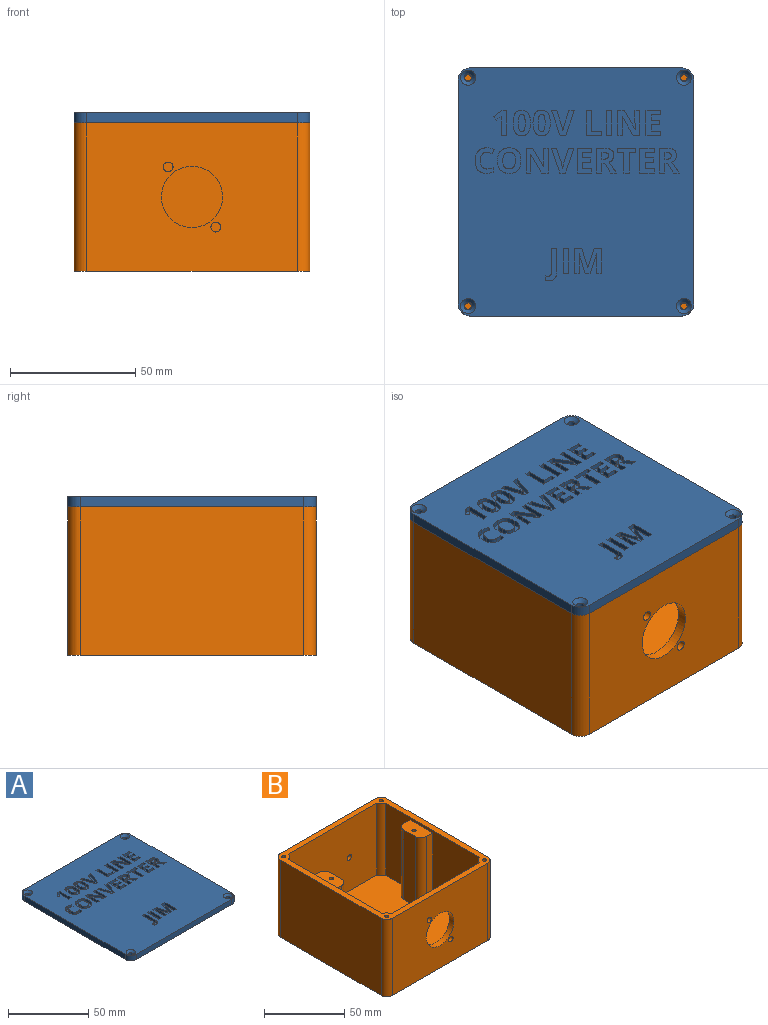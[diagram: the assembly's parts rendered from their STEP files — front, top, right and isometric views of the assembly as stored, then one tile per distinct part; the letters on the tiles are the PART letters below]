
ASSEMBLY  parts=2 mates=1
PART A: 287 faces, bbox 94x99x4 mm
  f0: plane 99x94mm, normal (0,0,1), area 8303.9mm2, adj f1,f2,f3,f8,f10,f11,f12,f13
  f1: plane 84x4mm, normal (0,1,0), area 336mm2, adj f0,f9,f10,f13
  f2: plane 89x4mm, normal (-1,0,0), area 356mm2, adj f0,f9,f10,f11
  f3: plane 84x4mm, normal (0,-1,0), area 336mm2, adj f0,f9,f11,f12
  f4: cylinder r=1.5mm len=3mm, axis (0,0,-1), area 23.6mm2, adj f9,f17
  f5: cylinder r=1.5mm len=3mm, axis (0,0,-1), area 23.6mm2, adj f9,f14
  f6: cylinder r=1.5mm len=3mm, axis (0,0,-1), area 23.6mm2, adj f9,f15
  f7: cylinder r=1.5mm len=3mm, axis (0,0,-1), area 23.6mm2, adj f9,f16
  f8: plane 89x4mm, normal (1,0,0), area 356mm2, adj f0,f9,f12,f13
  f9: plane 99x94mm, normal (0,0,-1), area 9256.3mm2, adj f1,f2,f3,f4,f5,f6,f7,f8
  f10: cylinder r=5mm len=5mm, axis (0,0,1), area 31.4mm2, adj f0,f1,f2,f9
  f11: cylinder r=5mm len=5mm, axis (0,0,-1), area 31.4mm2, adj f0,f2,f3,f9
  f12: cylinder r=5mm len=5mm, axis (0,0,1), area 31.4mm2, adj f0,f3,f8,f9
  f13: cylinder r=5mm len=5mm, axis (0,0,-1), area 31.4mm2, adj f0,f1,f8,f9
  f14: cone r=1.5mm half-angle=45deg, axis (0,0,1), area 30mm2, adj f0,f5
  f15: cone r=1.5mm half-angle=45deg, axis (0,0,1), area 30mm2, adj f0,f6
  f16: cone r=1.5mm half-angle=45deg, axis (0,0,1), area 30mm2, adj f0,f7
  f17: cone r=1.5mm half-angle=45deg, axis (0,0,1), area 30mm2, adj f0,f4
  f18: extruded ~2.18x2mm, area 4.5mm2, adj f0,f19,f27,f28
  f19: extruded ~2x0.97mm, area 2mm2, adj f0,f18,f20,f28
  f20: extruded ~2x1.22mm, area 2.5mm2, adj f0,f19,f21,f28
  f21: plane 5.9x2mm, normal (-0.95,-0.3,0), area 12.4mm2, adj f0,f20,f22,f28
  f22: plane 2.12x2mm, normal (0,-1,0), area 4.2mm2, adj f0,f21,f23,f28
  f23: plane 9.92x3.36mm, normal (0.95,0.32,0), area 20.9mm2, adj f0,f22,f24,f28
  f24: plane 2.29x2mm, normal (0,1,0), area 4.6mm2, adj f0,f23,f25,f28
  f25: plane 9.92x3.37mm, normal (-0.95,0.32,0), area 20.9mm2, adj f0,f24,f26,f28
  f26: plane 2.12x2mm, normal (0,-1,0), area 4.2mm2, adj f0,f25,f27,f28
  f27: plane 5.9x2mm, normal (0.95,-0.3,0), area 12.4mm2, adj f0,f18,f26,f28
  f28: plane 9.92x9.03mm, normal (0,0,1), area 37.9mm2, adj f18,f19,f20,f21,f22,f23,f24,f25
  f29: plane 2x1.72mm, normal (0,-1,0), area 3.4mm2, adj f0,f30,f38,f39
  f30: plane 3.19x2.54mm, normal (0.62,-0.78,0), area 8.2mm2, adj f0,f29,f31,f39
  f31: plane 2x1.26mm, normal (0.78,0.63,0), area 3.2mm2, adj f0,f30,f32,f39
  f32: plane 2x1.14mm, normal (-0.63,0.78,0), area 2.9mm2, adj f0,f31,f33,f39
  f33: extruded ~2x0.73mm, area 2mm2, adj f0,f32,f34,f39
  f34: plane 2x1.03mm, normal (1,-0.03,0), area 2.1mm2, adj f0,f33,f35,f39
  f35: plane 2x0.94mm, normal (1,-0.02,0), area 1.9mm2, adj f0,f34,f36,f39
  f36: plane 5.74x2mm, normal (1,0,0), area 11.5mm2, adj f0,f35,f37,f39
  f37: plane 2.1x2mm, normal (0,1,0), area 4.2mm2, adj f0,f36,f38,f39
  f38: plane 9.92x2mm, normal (-1,0,0), area 19.8mm2, adj f0,f29,f37,f39
  f39: plane 9.92x4.92mm, normal (0,0,1), area 25.4mm2, adj f29,f30,f31,f32,f33,f34,f35,f36
  f40: plane 3.8x2.37mm, normal (0.85,0.53,0), area 9mm2, adj f0,f41,f57,f59
  f41: plane 2.33x2mm, normal (0,1,0), area 4.7mm2, adj f0,f40,f42,f59
  f42: extruded ~4.32x2.92mm, area 10.4mm2, adj f0,f41,f43,f59
  f43: extruded ~2x1.36mm, area 3.5mm2, adj f0,f42,f44,f59
  f44: extruded ~2x1.56mm, area 3.3mm2, adj f0,f43,f45,f59
  f45: extruded ~2.24x2mm, area 5.1mm2, adj f0,f44,f46,f59
  f46: extruded ~2.99x2mm, area 6.3mm2, adj f0,f45,f47,f59
  f47: plane 2.89x2mm, normal (0,-1,0), area 5.8mm2, adj f0,f46,f48,f59
  f48: plane 9.92x2mm, normal (1,0,0), area 19.8mm2, adj f0,f47,f49,f59
  f49: plane 2.1x2mm, normal (0,1,0), area 4.2mm2, adj f0,f48,f50,f59
  f50: plane 3.8x2mm, normal (-1,0,0), area 7.6mm2, adj f0,f49,f57,f59
  f51: plane 2x0.64mm, normal (0,1,0), area 1.3mm2, adj f52,f58,f59,f285
  f52: extruded ~2x1.5mm, area 3.1mm2, adj f51,f53,f59,f285
  f53: extruded ~2x1mm, area 2.3mm2, adj f52,f54,f59,f285
  f54: extruded ~2x1.04mm, area 2.4mm2, adj f53,f55,f59,f285
  f55: extruded ~2x1.47mm, area 3.1mm2, adj f54,f56,f59,f285
  f56: plane 2x0.68mm, normal (0,-1,0), area 1.4mm2, adj f55,f58,f59,f285
  f57: plane 2x1.12mm, normal (0,1,0), area 2.2mm2, adj f0,f40,f50,f59
  f58: plane 2.68x2mm, normal (-1,0,0), area 5.4mm2, adj f51,f56,f59,f285
  f59: plane 9.92x7.92mm, normal (0,0,1), area 48mm2, adj f40,f41,f42,f43,f44,f45,f46,f47
  f60: plane 3.8x2.37mm, normal (0.85,0.53,0), area 9mm2, adj f0,f61,f77,f79
  f61: plane 2.33x2mm, normal (0,1,0), area 4.7mm2, adj f0,f60,f62,f79
  f62: extruded ~4.32x2.92mm, area 10.4mm2, adj f0,f61,f63,f79
  f63: extruded ~2x1.36mm, area 3.5mm2, adj f0,f62,f64,f79
  f64: extruded ~2x1.56mm, area 3.3mm2, adj f0,f63,f65,f79
  f65: extruded ~2.24x2mm, area 5.1mm2, adj f0,f64,f66,f79
  f66: extruded ~2.99x2mm, area 6.3mm2, adj f0,f65,f67,f79
  f67: plane 2.89x2mm, normal (0,-1,0), area 5.8mm2, adj f0,f66,f68,f79
  f68: plane 9.92x2mm, normal (1,0,0), area 19.8mm2, adj f0,f67,f69,f79
  f69: plane 2.1x2mm, normal (0,1,0), area 4.2mm2, adj f0,f68,f70,f79
  f70: plane 3.8x2mm, normal (-1,0,0), area 7.6mm2, adj f0,f69,f77,f79
  f71: plane 2x0.64mm, normal (0,1,0), area 1.3mm2, adj f72,f78,f79,f286
  f72: extruded ~2x1.5mm, area 3.1mm2, adj f71,f73,f79,f286
  f73: extruded ~2x1mm, area 2.3mm2, adj f72,f74,f79,f286
  f74: extruded ~2x1.04mm, area 2.4mm2, adj f73,f75,f79,f286
  f75: extruded ~2x1.47mm, area 3.1mm2, adj f74,f76,f79,f286
  f76: plane 2x0.68mm, normal (0,-1,0), area 1.4mm2, adj f75,f78,f79,f286
  f77: plane 2x1.12mm, normal (0,1,0), area 2.2mm2, adj f0,f60,f70,f79
  f78: plane 2.68x2mm, normal (-1,0,0), area 5.4mm2, adj f71,f76,f79,f286
  f79: plane 9.92x7.92mm, normal (0,0,1), area 48mm2, adj f60,f61,f62,f63,f64,f65,f66,f67
  f80: plane 2x1.74mm, normal (-1,0,0), area 3.5mm2, adj f0,f81,f85,f86
  f81: plane 4.02x2mm, normal (0,-1,0), area 8mm2, adj f0,f80,f82,f86
  f82: plane 8.18x2mm, normal (-1,0,0), area 16.4mm2, adj f0,f81,f83,f86
  f83: plane 2.1x2mm, normal (0,-1,0), area 4.2mm2, adj f0,f82,f84,f86
  f84: plane 9.92x2mm, normal (1,0,0), area 19.8mm2, adj f0,f83,f85,f86
  f85: plane 6.12x2mm, normal (0,1,0), area 12.2mm2, adj f0,f80,f84,f86
  f86: plane 9.92x6.12mm, normal (0,0,1), area 27.8mm2, adj f80,f81,f82,f83,f84,f85
  f87: plane 9.92x2mm, normal (-1,0,0), area 19.8mm2, adj f0,f88,f90,f91
  f88: plane 2.1x2mm, normal (0,-1,0), area 4.2mm2, adj f0,f87,f89,f91
  f89: plane 9.92x2mm, normal (1,0,0), area 19.8mm2, adj f0,f88,f90,f91
  f90: plane 2.1x2mm, normal (0,1,0), area 4.2mm2, adj f0,f87,f89,f91
  f91: plane 9.92x2.1mm, normal (0,0,1), area 20.9mm2, adj f87,f88,f89,f90
  f92: plane 2x1.89mm, normal (0,-1,0), area 3.8mm2, adj f0,f93,f105,f106
  f93: plane 4.69x2mm, normal (1,0,0), area 9.4mm2, adj f0,f92,f94,f106
  f94: extruded ~2.73x2mm, area 5.5mm2, adj f0,f93,f95,f106
  f95: plane 2x0.05mm, normal (0,-1,0), area 0.1mm2, adj f0,f94,f96,f106
  f96: plane 7.43x4.31mm, normal (-0.87,-0.5,0), area 17.2mm2, adj f0,f95,f97,f106
  f97: plane 2.65x2mm, normal (0,-1,0), area 5.3mm2, adj f0,f96,f98,f106
  f98: plane 9.92x2mm, normal (1,0,0), area 19.8mm2, adj f0,f97,f99,f106
  f99: plane 2x1.88mm, normal (0,1,0), area 3.8mm2, adj f0,f98,f100,f106
  f100: plane 4.67x2mm, normal (-1,0,0), area 9.3mm2, adj f0,f99,f101,f106
  f101: extruded ~2.83x2mm, area 5.7mm2, adj f0,f100,f102,f106
  f102: plane 2x0.06mm, normal (0,1,0), area 0.1mm2, adj f0,f101,f103,f106
  f103: plane 7.5x4.31mm, normal (0.87,0.5,0), area 17.3mm2, adj f0,f102,f104,f106
  f104: plane 2.67x2mm, normal (0,1,0), area 5.3mm2, adj f0,f103,f105,f106
  f105: plane 9.92x2mm, normal (-1,0,0), area 19.8mm2, adj f0,f92,f104,f106
  f106: plane 9.92x8.8mm, normal (0,0,1), area 55.7mm2, adj f92,f93,f94,f95,f96,f97,f98,f99
  f107: plane 3.61x2mm, normal (0,-1,0), area 7.2mm2, adj f0,f108,f118,f119
  f108: plane 2.56x2mm, normal (-1,0,0), area 5.1mm2, adj f0,f107,f109,f119
  f109: plane 3.36x2mm, normal (0,1,0), area 6.7mm2, adj f0,f108,f110,f119
  f110: plane 2x1.72mm, normal (-1,0,0), area 3.4mm2, adj f0,f109,f111,f119
  f111: plane 3.36x2mm, normal (0,-1,0), area 6.7mm2, adj f0,f110,f112,f119
  f112: plane 2.18x2mm, normal (-1,0,0), area 4.4mm2, adj f0,f111,f113,f119
  f113: plane 3.61x2mm, normal (0,1,0), area 7.2mm2, adj f0,f112,f114,f119
  f114: plane 2x1.72mm, normal (-1,0,0), area 3.4mm2, adj f0,f113,f115,f119
  f115: plane 5.71x2mm, normal (0,-1,0), area 11.4mm2, adj f0,f114,f116,f119
  f116: plane 9.92x2mm, normal (1,0,0), area 19.8mm2, adj f0,f115,f117,f119
  f117: plane 5.71x2mm, normal (0,1,0), area 11.4mm2, adj f0,f116,f118,f119
  f118: plane 2x1.74mm, normal (-1,0,0), area 3.5mm2, adj f0,f107,f117,f119
  f119: plane 9.92x5.71mm, normal (0,0,1), area 39.1mm2, adj f107,f108,f109,f110,f111,f112,f113,f114
  f120: extruded ~2x1.12mm, area 2.4mm2, adj f0,f121,f134,f135
  f121: plane 2x1.71mm, normal (-0.93,0.37,0), area 3.7mm2, adj f0,f120,f122,f135
  f122: extruded ~2.9x2mm, area 6mm2, adj f0,f121,f123,f135
  f123: extruded ~2.47x2mm, area 5.2mm2, adj f0,f122,f124,f135
  f124: extruded ~2x1.78mm, area 4.9mm2, adj f0,f123,f125,f135
  f125: extruded ~2.71x2mm, area 5.6mm2, adj f0,f124,f126,f135
  f126: extruded ~3.77x2mm, area 8mm2, adj f0,f125,f127,f135
  f127: extruded ~3.31x2mm, area 7.4mm2, adj f0,f126,f128,f135
  f128: extruded ~2.73x2mm, area 5.6mm2, adj f0,f127,f129,f135
  f129: plane 2x1.76mm, normal (-1,0,0), area 3.5mm2, adj f0,f128,f130,f135
  f130: extruded ~2.53x2mm, area 5.2mm2, adj f0,f129,f131,f135
  f131: extruded ~3.32x2.49mm, area 9.5mm2, adj f0,f130,f132,f135
  f132: extruded ~2.49x2mm, area 5.2mm2, adj f0,f131,f133,f135
  f133: extruded ~2x1.84mm, area 4.3mm2, adj f0,f132,f134,f135
  f134: extruded ~2x1.1mm, area 2.3mm2, adj f0,f120,f133,f135
  f135: plane 10.19x7.55mm, normal (0,0,1), area 34.5mm2, adj f120,f121,f122,f123,f124,f125,f126,f127
  f136: plane 2x1.89mm, normal (0,-1,0), area 3.8mm2, adj f0,f137,f149,f150
  f137: plane 4.69x2mm, normal (1,0,0), area 9.4mm2, adj f0,f136,f138,f150
  f138: extruded ~2.73x2mm, area 5.5mm2, adj f0,f137,f139,f150
  f139: plane 2x0.05mm, normal (0,-1,0), area 0.1mm2, adj f0,f138,f140,f150
  f140: plane 7.43x4.31mm, normal (-0.87,-0.5,0), area 17.2mm2, adj f0,f139,f141,f150
  f141: plane 2.65x2mm, normal (0,-1,0), area 5.3mm2, adj f0,f140,f142,f150
  f142: plane 9.92x2mm, normal (1,0,0), area 19.8mm2, adj f0,f141,f143,f150
  f143: plane 2x1.88mm, normal (0,1,0), area 3.8mm2, adj f0,f142,f144,f150
  f144: plane 4.67x2mm, normal (-1,0,0), area 9.3mm2, adj f0,f143,f145,f150
  f145: extruded ~2.83x2mm, area 5.7mm2, adj f0,f144,f146,f150
  f146: plane 2x0.06mm, normal (0,1,0), area 0.1mm2, adj f0,f145,f147,f150
  f147: plane 7.5x4.31mm, normal (0.87,0.5,0), area 17.3mm2, adj f0,f146,f148,f150
  f148: plane 2.67x2mm, normal (0,1,0), area 5.3mm2, adj f0,f147,f149,f150
  f149: plane 9.92x2mm, normal (-1,0,0), area 19.8mm2, adj f0,f136,f148,f150
  f150: plane 9.92x8.8mm, normal (0,0,1), area 55.7mm2, adj f136,f137,f138,f139,f140,f141,f142,f143
  f151: extruded ~2.18x2mm, area 4.5mm2, adj f0,f152,f160,f161
  f152: extruded ~2x0.97mm, area 2mm2, adj f0,f151,f153,f161
  f153: extruded ~2x1.22mm, area 2.5mm2, adj f0,f152,f154,f161
  f154: plane 5.9x2mm, normal (-0.95,-0.3,0), area 12.4mm2, adj f0,f153,f155,f161
  f155: plane 2.12x2mm, normal (0,-1,0), area 4.2mm2, adj f0,f154,f156,f161
  f156: plane 9.92x3.36mm, normal (0.95,0.32,0), area 20.9mm2, adj f0,f155,f157,f161
  f157: plane 2.29x2mm, normal (0,1,0), area 4.6mm2, adj f0,f156,f158,f161
  f158: plane 9.92x3.37mm, normal (-0.95,0.32,0), area 20.9mm2, adj f0,f157,f159,f161
  f159: plane 2.12x2mm, normal (0,-1,0), area 4.2mm2, adj f0,f158,f160,f161
  f160: plane 5.9x2mm, normal (0.95,-0.3,0), area 12.4mm2, adj f0,f151,f159,f161
  f161: plane 9.92x9.03mm, normal (0,0,1), area 37.9mm2, adj f151,f152,f153,f154,f155,f156,f157,f158
  f162: plane 3.61x2mm, normal (0,-1,0), area 7.2mm2, adj f0,f163,f173,f174
  f163: plane 2.56x2mm, normal (-1,0,0), area 5.1mm2, adj f0,f162,f164,f174
  f164: plane 3.36x2mm, normal (0,1,0), area 6.7mm2, adj f0,f163,f165,f174
  f165: plane 2x1.72mm, normal (-1,0,0), area 3.4mm2, adj f0,f164,f166,f174
  f166: plane 3.36x2mm, normal (0,-1,0), area 6.7mm2, adj f0,f165,f167,f174
  f167: plane 2.18x2mm, normal (-1,0,0), area 4.4mm2, adj f0,f166,f168,f174
  f168: plane 3.61x2mm, normal (0,1,0), area 7.2mm2, adj f0,f167,f169,f174
  f169: plane 2x1.72mm, normal (-1,0,0), area 3.4mm2, adj f0,f168,f170,f174
  f170: plane 5.71x2mm, normal (0,-1,0), area 11.4mm2, adj f0,f169,f171,f174
  f171: plane 9.92x2mm, normal (1,0,0), area 19.8mm2, adj f0,f170,f172,f174
  f172: plane 5.71x2mm, normal (0,1,0), area 11.4mm2, adj f0,f171,f173,f174
  f173: plane 2x1.74mm, normal (-1,0,0), area 3.5mm2, adj f0,f162,f172,f174
  f174: plane 9.92x5.71mm, normal (0,0,1), area 39.1mm2, adj f162,f163,f164,f165,f166,f167,f168,f169
  f175: plane 7.76x2.56mm, normal (-0.95,0.31,0), area 16.3mm2, adj f0,f176,f193,f194
  f176: plane 2x0.06mm, normal (0,1,0), area 0.1mm2, adj f0,f175,f177,f194
  f177: extruded ~2.3x2mm, area 4.6mm2, adj f0,f176,f178,f194
  f178: extruded ~2x0.77mm, area 1.5mm2, adj f0,f177,f179,f194
  f179: plane 4.69x2mm, normal (1,0,0), area 9.4mm2, adj f0,f178,f180,f194
  f180: plane 2x1.96mm, normal (0,1,0), area 3.9mm2, adj f0,f179,f181,f194
  f181: plane 9.92x2mm, normal (-1,0,0), area 19.8mm2, adj f0,f180,f182,f194
  f182: plane 2.86x2mm, normal (0,-1,0), area 5.7mm2, adj f0,f181,f183,f194
  f183: plane 7.58x2.49mm, normal (0.95,-0.31,0), area 16mm2, adj f0,f182,f184,f194
  f184: plane 2x0.04mm, normal (0,-1,0), area 0.1mm2, adj f0,f183,f185,f194
  f185: plane 7.58x2.35mm, normal (-0.96,-0.3,0), area 15.9mm2, adj f0,f184,f186,f194
  f186: plane 2.86x2mm, normal (0,-1,0), area 5.7mm2, adj f0,f185,f187,f194
  f187: plane 9.92x2mm, normal (1,0,0), area 19.8mm2, adj f0,f186,f188,f194
  f188: plane 2x1.88mm, normal (0,1,0), area 3.8mm2, adj f0,f187,f189,f194
  f189: plane 4.61x2mm, normal (-1,0,0), area 9.2mm2, adj f0,f188,f190,f194
  f190: extruded ~3.17x2mm, area 6.3mm2, adj f0,f189,f191,f194
  f191: plane 2x0.06mm, normal (0,1,0), area 0.1mm2, adj f0,f190,f192,f194
  f192: plane 7.78x2.39mm, normal (0.96,0.29,0), area 16.3mm2, adj f0,f191,f193,f194
  f193: plane 2x1.93mm, normal (0,1,0), area 3.9mm2, adj f0,f175,f192,f194
  f194: plane 10.6x9.92mm, normal (0,0,1), area 67.8mm2, adj f175,f176,f177,f178,f179,f180,f181,f182
  f195: extruded ~2x1.06mm, area 2.8mm2, adj f196,f209,f211,f212
  f196: extruded ~2x1.05mm, area 2.8mm2, adj f195,f197,f211,f212
  f197: extruded ~2.62x2mm, area 5.3mm2, adj f196,f198,f211,f212
  f198: extruded ~2.6x2mm, area 5.3mm2, adj f197,f199,f211,f212
  f199: extruded ~2x1.06mm, area 2.8mm2, adj f198,f200,f211,f212
  f200: extruded ~2x1.06mm, area 2.8mm2, adj f199,f201,f211,f212
  f201: extruded ~2.61x2mm, area 5.3mm2, adj f200,f209,f211,f212
  f202: extruded ~2.59x2mm, area 6.1mm2, adj f0,f203,f210,f211
  f203: extruded ~2.61x2mm, area 6mm2, adj f0,f202,f204,f211
  f204: extruded ~3.87x2mm, area 8mm2, adj f0,f203,f205,f211
  f205: extruded ~3.8x2mm, area 7.9mm2, adj f0,f204,f206,f211
  f206: extruded ~2.59x2mm, area 6mm2, adj f0,f205,f207,f211
  f207: extruded ~2.62x2mm, area 6.1mm2, adj f0,f206,f208,f211
  f208: extruded ~3.84x2mm, area 8mm2, adj f0,f207,f210,f211
  f209: extruded ~2.62x2mm, area 5.3mm2, adj f195,f201,f211,f212
  f210: extruded ~3.81x2mm, area 7.9mm2, adj f0,f202,f208,f211
  f211: plane 10.21x6.93mm, normal (0,0,1), area 43mm2, adj f195,f196,f197,f198,f199,f200,f201,f202
  f212: plane 6.82x2.76mm, normal (0,0,1), area 16mm2, adj f195,f196,f197,f198,f199,f200,f201,f209
  f213: extruded ~2x1.06mm, area 2.8mm2, adj f214,f227,f229,f230
  f214: extruded ~2x1.05mm, area 2.8mm2, adj f213,f215,f229,f230
  f215: extruded ~2.62x2mm, area 5.3mm2, adj f214,f216,f229,f230
  f216: extruded ~2.6x2mm, area 5.3mm2, adj f215,f217,f229,f230
  f217: extruded ~2x1.06mm, area 2.8mm2, adj f216,f218,f229,f230
  f218: extruded ~2x1.06mm, area 2.8mm2, adj f217,f219,f229,f230
  f219: extruded ~2.61x2mm, area 5.3mm2, adj f218,f227,f229,f230
  f220: extruded ~2.59x2mm, area 6.1mm2, adj f0,f221,f228,f229
  f221: extruded ~2.61x2mm, area 6mm2, adj f0,f220,f222,f229
  f222: extruded ~3.87x2mm, area 8mm2, adj f0,f221,f223,f229
  f223: extruded ~3.8x2mm, area 7.9mm2, adj f0,f222,f224,f229
  f224: extruded ~2.59x2mm, area 6mm2, adj f0,f223,f225,f229
  f225: extruded ~2.62x2mm, area 6.1mm2, adj f0,f224,f226,f229
  f226: extruded ~3.84x2mm, area 8mm2, adj f0,f225,f228,f229
  f227: extruded ~2.62x2mm, area 5.3mm2, adj f213,f219,f229,f230
  f228: extruded ~3.81x2mm, area 7.9mm2, adj f0,f220,f226,f229
  f229: plane 10.21x6.93mm, normal (0,0,1), area 43mm2, adj f213,f214,f215,f216,f217,f218,f219,f220
  f230: plane 6.82x2.76mm, normal (0,0,1), area 16mm2, adj f213,f214,f215,f216,f217,f218,f219,f227
  f231: extruded ~2x1.89mm, area 4.3mm2, adj f232,f243,f245,f246
  f232: extruded ~3.35x2.5mm, area 9.5mm2, adj f231,f233,f245,f246
  f233: extruded ~3.34x2.52mm, area 9.5mm2, adj f232,f234,f245,f246
  f234: extruded ~2x1.88mm, area 4.3mm2, adj f233,f235,f245,f246
  f235: extruded ~2.5x2mm, area 5.2mm2, adj f234,f243,f245,f246
  f236: extruded ~3.5x2mm, area 7.7mm2, adj f0,f237,f244,f245
  f237: extruded ~3.51x2mm, area 7.7mm2, adj f0,f236,f238,f245
  f238: extruded ~3.78x2mm, area 8.1mm2, adj f0,f237,f239,f245
  f239: extruded ~3.8x2mm, area 8.2mm2, adj f0,f238,f240,f245
  f240: extruded ~3.5x2mm, area 7.7mm2, adj f0,f239,f241,f245
  f241: extruded ~3.5x2mm, area 7.7mm2, adj f0,f240,f242,f245
  f242: extruded ~3.79x2mm, area 8.1mm2, adj f0,f241,f244,f245
  f243: extruded ~2.5x2mm, area 5.3mm2, adj f231,f235,f245,f246
  f244: extruded ~3.78x2mm, area 8.1mm2, adj f0,f236,f242,f245
  f245: plane 10.21x9.44mm, normal (0,0,1), area 51.5mm2, adj f231,f232,f233,f234,f235,f236,f237,f238
  f246: plane 6.69x5.03mm, normal (0,0,1), area 28mm2, adj f231,f232,f233,f234,f235,f243
  f247: plane 9.92x2mm, normal (-1,0,0), area 19.8mm2, adj f0,f248,f250,f251
  f248: plane 2.1x2mm, normal (0,-1,0), area 4.2mm2, adj f0,f247,f249,f251
  f249: plane 9.92x2mm, normal (1,0,0), area 19.8mm2, adj f0,f248,f250,f251
  f250: plane 2.1x2mm, normal (0,1,0), area 4.2mm2, adj f0,f247,f249,f251
  f251: plane 9.92x2.1mm, normal (0,0,1), area 20.9mm2, adj f247,f248,f249,f250
  f252: extruded ~2.65x2mm, area 5.6mm2, adj f0,f253,f261,f262
  f253: plane 9.28x2mm, normal (-1,0,0), area 18.6mm2, adj f0,f252,f254,f262
  f254: plane 2.1x2mm, normal (0,-1,0), area 4.2mm2, adj f0,f253,f255,f262
  f255: plane 9.29x2mm, normal (1,0,0), area 18.6mm2, adj f0,f254,f256,f262
  f256: extruded ~2x1.35mm, area 2.8mm2, adj f0,f255,f257,f262
  f257: extruded ~2x0.99mm, area 2.3mm2, adj f0,f256,f258,f262
  f258: extruded ~2x0.99mm, area 2mm2, adj f0,f257,f259,f262
  f259: plane 2x1.75mm, normal (1,0,0), area 3.5mm2, adj f0,f258,f260,f262
  f260: extruded ~2x1.24mm, area 2.5mm2, adj f0,f259,f261,f262
  f261: extruded ~2.35x2mm, area 5.2mm2, adj f0,f252,f260,f262
  f262: plane 12.83x4.38mm, normal (0,0,1), area 29.4mm2, adj f252,f253,f254,f255,f256,f257,f258,f259
  f263: plane 3.61x2mm, normal (0,-1,0), area 7.2mm2, adj f0,f264,f274,f275
  f264: plane 2.56x2mm, normal (-1,0,0), area 5.1mm2, adj f0,f263,f265,f275
  f265: plane 3.36x2mm, normal (0,1,0), area 6.7mm2, adj f0,f264,f266,f275
  f266: plane 2x1.72mm, normal (-1,0,0), area 3.4mm2, adj f0,f265,f267,f275
  f267: plane 3.36x2mm, normal (0,-1,0), area 6.7mm2, adj f0,f266,f268,f275
  f268: plane 2.18x2mm, normal (-1,0,0), area 4.4mm2, adj f0,f267,f269,f275
  f269: plane 3.61x2mm, normal (0,1,0), area 7.2mm2, adj f0,f268,f270,f275
  f270: plane 2x1.72mm, normal (-1,0,0), area 3.4mm2, adj f0,f269,f271,f275
  f271: plane 5.71x2mm, normal (0,-1,0), area 11.4mm2, adj f0,f270,f272,f275
  f272: plane 9.92x2mm, normal (1,0,0), area 19.8mm2, adj f0,f271,f273,f275
  f273: plane 5.71x2mm, normal (0,1,0), area 11.4mm2, adj f0,f272,f274,f275
  f274: plane 2x1.74mm, normal (-1,0,0), area 3.5mm2, adj f0,f263,f273,f275
  f275: plane 9.92x5.71mm, normal (0,0,1), area 39.1mm2, adj f263,f264,f265,f266,f267,f268,f269,f270
  f276: plane 2.69x2mm, normal (0,1,0), area 5.4mm2, adj f0,f277,f283,f284
  f277: plane 2x1.75mm, normal (-1,0,0), area 3.5mm2, adj f0,f276,f278,f284
  f278: plane 7.49x2mm, normal (0,-1,0), area 15mm2, adj f0,f277,f279,f284
  f279: plane 2x1.75mm, normal (1,0,0), area 3.5mm2, adj f0,f278,f280,f284
  f280: plane 2.69x2mm, normal (0,1,0), area 5.4mm2, adj f0,f279,f281,f284
  f281: plane 8.17x2mm, normal (1,0,0), area 16.3mm2, adj f0,f280,f282,f284
  f282: plane 2.1x2mm, normal (0,1,0), area 4.2mm2, adj f0,f281,f283,f284
  f283: plane 8.17x2mm, normal (-1,0,0), area 16.3mm2, adj f0,f276,f282,f284
  f284: plane 9.92x7.49mm, normal (0,0,1), area 30.3mm2, adj f276,f277,f278,f279,f280,f281,f282,f283
  f285: plane 2.68x2.62mm, normal (0,0,1), area 6.2mm2, adj f51,f52,f53,f54,f55,f56,f58
  f286: plane 2.68x2.62mm, normal (0,0,1), area 6.2mm2, adj f71,f72,f73,f74,f75,f76,f78
PART B: 48 faces, bbox 94x99x59 mm
  f0: plane 53x5.5mm, normal (0,1,0), area 291.5mm2, adj f11,f15,f25,f33
  f1: plane 53x10mm, normal (-1,0,0), area 530mm2, adj f15,f25,f33,f34
  f2: plane 53x5.5mm, normal (0,-1,0), area 291.5mm2, adj f11,f15,f25,f34
  f3: plane 53x5.5mm, normal (0,-1,0), area 291.5mm2, adj f13,f15,f26,f37
  f4: plane 53x10mm, normal (1,0,0), area 530mm2, adj f15,f26,f37,f38
  f5: plane 53x5.5mm, normal (0,1,0), area 291.5mm2, adj f13,f15,f26,f38
  f6: plane 99x94mm, normal (0,0,1), area 1482.8mm2, adj f7,f8,f9,f10,f11,f12,f13,f14
  f7: plane 84x59mm, normal (0,1,0), area 4933.3mm2, adj f6,f16,f39,f42,f46,f47
  f8: plane 89x59mm, normal (-1,0,0), area 5251mm2, adj f6,f16,f39,f40
  f9: plane 84x59mm, normal (0,-1,0), area 4464.5mm2, adj f6,f16,f40,f41,f43,f44,f45
  f10: plane 78x55mm, normal (0,-1,0), area 4267.3mm2, adj f6,f15,f31,f32,f46,f47
  f11: plane 83x55mm, normal (-1,0,0), area 3505mm2, adj f0,f2,f6,f15,f25,f32,f35
  f12: plane 78x55mm, normal (0,1,0), area 3798.5mm2, adj f6,f15,f35,f36,f43,f44,f45
  f13: plane 83x55mm, normal (1,0,0), area 3505mm2, adj f3,f5,f6,f15,f26,f31,f36
  f14: plane 89x59mm, normal (1,0,0), area 5251mm2, adj f6,f16,f41,f42
  f15: plane 91x86mm, normal (0,0,1), area 7382mm2, adj f0,f1,f2,f3,f4,f5,f10,f11
  f16: plane 99x94mm, normal (0,0,-1), area 9284.5mm2, adj f7,f8,f9,f14,f39,f40,f41,f42
  f17: cylinder r=1.3mm len=30mm, axis (0,0,1), area 245mm2, adj f6,f18
  f18: plane 2.6x2.6mm, normal (0,0,1), area 5.3mm2, adj f17
  f19: cylinder r=1.3mm len=30mm, axis (0,0,1), area 245mm2, adj f6,f20
  f20: plane 2.6x2.6mm, normal (0,0,1), area 5.3mm2, adj f19
  f21: cylinder r=1.3mm len=30mm, axis (0,0,1), area 245mm2, adj f6,f22
  f22: plane 2.6x2.6mm, normal (0,0,1), area 5.3mm2, adj f21
  f23: cylinder r=1.3mm len=30mm, axis (0,0,1), area 245mm2, adj f6,f24
  f24: plane 2.6x2.6mm, normal (0,0,1), area 5.3mm2, adj f23
  f25: plane 20x10.5mm, normal (0,0,1), area 194mm2, adj f0,f1,f2,f11,f28,f33,f34
  f26: plane 20x10.5mm, normal (0,0,1), area 194mm2, adj f3,f4,f5,f13,f30,f37,f38
  f27: plane 2.6x2.6mm, normal (0,0,1), area 5.3mm2, adj f28
  f28: cylinder r=1.3mm len=28mm, axis (0,0,1), area 228.7mm2, adj f25,f27
  f29: plane 2.6x2.6mm, normal (0,0,1), area 5.3mm2, adj f30
  f30: cylinder r=1.3mm len=28mm, axis (0,0,1), area 228.7mm2, adj f26,f29
  f31: cylinder r=5mm len=55mm, axis (0,0,-1), area 330.7mm2, adj f6,f10,f13,f15
  f32: cylinder r=5mm len=55mm, axis (0,0,-1), area 330.7mm2, adj f6,f10,f11,f15
  f33: cylinder r=5mm len=53mm, axis (0,0,-1), area 416.3mm2, adj f0,f1,f15,f25
  f34: cylinder r=5mm len=53mm, axis (0,0,-1), area 416.3mm2, adj f1,f2,f15,f25
  f35: cylinder r=5mm len=55mm, axis (0,0,-1), area 330.7mm2, adj f6,f11,f12,f15
  f36: cylinder r=5mm len=55mm, axis (0,0,-1), area 330.7mm2, adj f6,f12,f13,f15
  f37: cylinder r=5mm len=53mm, axis (0,0,-1), area 416.3mm2, adj f3,f4,f15,f26
  f38: cylinder r=5mm len=53mm, axis (0,0,-1), area 416.3mm2, adj f4,f5,f15,f26
  f39: cylinder r=5mm len=59mm, axis (0,0,1), area 463.4mm2, adj f6,f7,f8,f16
  f40: cylinder r=5mm len=59mm, axis (0,0,-1), area 463.4mm2, adj f6,f8,f9,f16
  f41: cylinder r=5mm len=59mm, axis (0,0,1), area 463.4mm2, adj f6,f9,f14,f16
  f42: cylinder r=5mm len=59mm, axis (0,0,-1), area 463.4mm2, adj f6,f7,f14,f16
  f43: cylinder r=1.95mm len=4mm, axis (0,-1,0), area 49mm2, adj f9,f12
  f44: cylinder r=12.2mm len=24.4mm, axis (0,-1,0), area 306.6mm2, adj f9,f12
  f45: cylinder r=1.95mm len=4mm, axis (0,-1,0), area 49mm2, adj f9,f12
  f46: cylinder r=1.9mm len=4mm, axis (0,1,0), area 47.8mm2, adj f7,f10
  f47: cylinder r=1.9mm len=4mm, axis (0,1,0), area 47.8mm2, adj f7,f10
PLACE A t=(-0.5,0,55)mm
PLACE B t=(-1,0,0)mm
MATE cylindrical A.f7 <-> B.f19  axis (0,0,-1) through (-44,-45.5,55)mm
